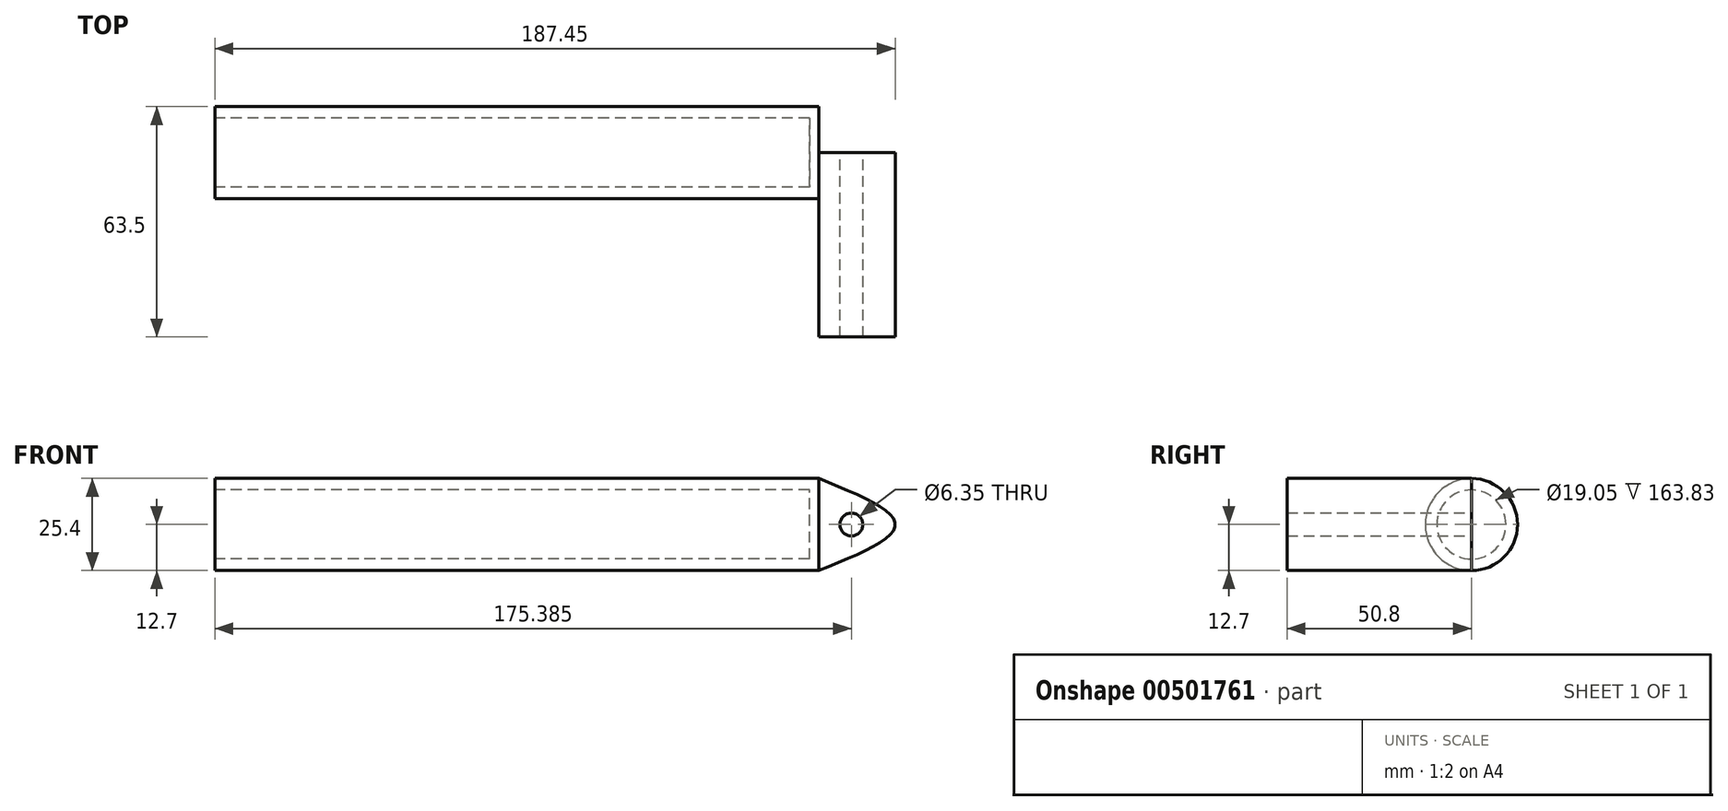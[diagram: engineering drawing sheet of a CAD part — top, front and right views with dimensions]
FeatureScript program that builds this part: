
annotation { "Feature Type Name" : "Feature", "Feature Type Description" : "" }
export const myFeature = defineFeature(function(context is Context, id is Id, definition is map)
    precondition{}
    {
        {
            var Q0;
            Q0=qCreatedBy(makeId("Right.planeOp"),FACE);
            var sketch = newSketch(context, id + "F0", { "sketchPlane" : qUnion([Q0])});
            skCircle(sketch, "E0", {"center": v(0, 0) * mm, "radius": 12.7 * mm});
            skCircle(sketch, "E1", {"center": v(0, 0) * mm, "radius": 9.53 * mm});
            skSolve(sketch);
        }
        {
            var Q0;
            Q0 = qSketchRegion(id + "F0", true);
            extrude(context, id + "F1", {"entities" : qUnion([Q0]), "endBound" : BoundingType.SYMMETRIC, "depth" : 115.57 * mm});
        }
        {
            var Q0;
            Q0=makeQuery(id+"F1.opExtrude","CAP_FACE",FACE,{"disambiguationData":[OSD([sQuery(id+"F0.wireOp",EDGE,"E0"),sQuery(id+"F0.wireOp",EDGE,"E1")])],"isStart":false});
            var sketch = newSketch(context, id + "F2", { "sketchPlane" : qUnion([Q0])});
            skCircle(sketch, "E2", {"center": v(0, 0) * mm, "radius": 12.7 * mm});
            skSolve(sketch);
        }
        {
            var Q0;
            Q0 = qSketchRegion(id + "F2", true);
            extrude(context, id + "F3", {"entities" : qUnion([Q0]), "operationType" : NewBodyOperationType.ADD, "oppositeDirection" : true, "depth" : 2.54 * mm});
        }
        {
            var Q0;
            Q0=qCreatedBy(makeId("Front.planeOp"),FACE);
            var sketch = newSketch(context, id + "F4", { "sketchPlane" : qUnion([Q0])});
            skLineSegment(sketch, "E3", {"start": v(0, 0) * mm, "end": v(57.79, 0) * mm});
            skLineSegment(sketch, "E4", {"start": v(57.79, 0) * mm, "end": v(57.79, 12.7) * mm});
            skLineSegment(sketch, "E5", {"start": v(57.79, 12.7) * mm, "end": v(57.79, -12.7) * mm});
            skFitSpline(sketch, "E6", {"points": [v(57.79, 12.7) * mm, v(57.79, -12.7) * mm], "startDerivative": vector(0, -25.4) * mm, "endDerivative": vector(0, -25.4) * mm});
            skFitSpline(sketch, "E7", {"points": [v(57.79, 12.7) * mm, v(78.86, 0) * mm, v(57.79, -12.7) * mm], "startDerivative": vector(63.23, -25.4) * mm, "endDerivative": vector(-63.23, -25.4) * mm});
            skCircle(sketch, "E8", {"center": v(66.8, 0) * mm, "radius": 3.18 * mm});
            skSolve(sketch);
        }
        {
            var Q0;
            Q0 = qSketchRegion(id + "F4", true);
            extrude(context, id + "F5", {"entities" : qUnion([Q0]), "operationType" : NewBodyOperationType.ADD, "depth" : 50.8 * mm});
        }
        {
            var Q0;
            Q0=makeQuery(id+"F1.opExtrude","CAP_FACE",FACE,{"disambiguationData":[OSD([sQuery(id+"F0.wireOp",EDGE,"E0"),sQuery(id+"F0.wireOp",EDGE,"E1")])],"isStart":true});
            var sketch = newSketch(context, id + "F6", { "sketchPlane" : qUnion([Q0])});
            skCircle(sketch, "E9", {"center": v(0, 0) * mm, "radius": 12.7 * mm});
            skCircle(sketch, "E10", {"center": v(0, 0) * mm, "radius": 9.53 * mm});
            skSolve(sketch);
        }
        {
            var Q0;
            Q0 = qSketchRegion(id + "F6", true);
            extrude(context, id + "F7", {"entities" : qUnion([Q0]), "operationType" : NewBodyOperationType.ADD, "depth" : 50.8 * mm});
        }
    });
